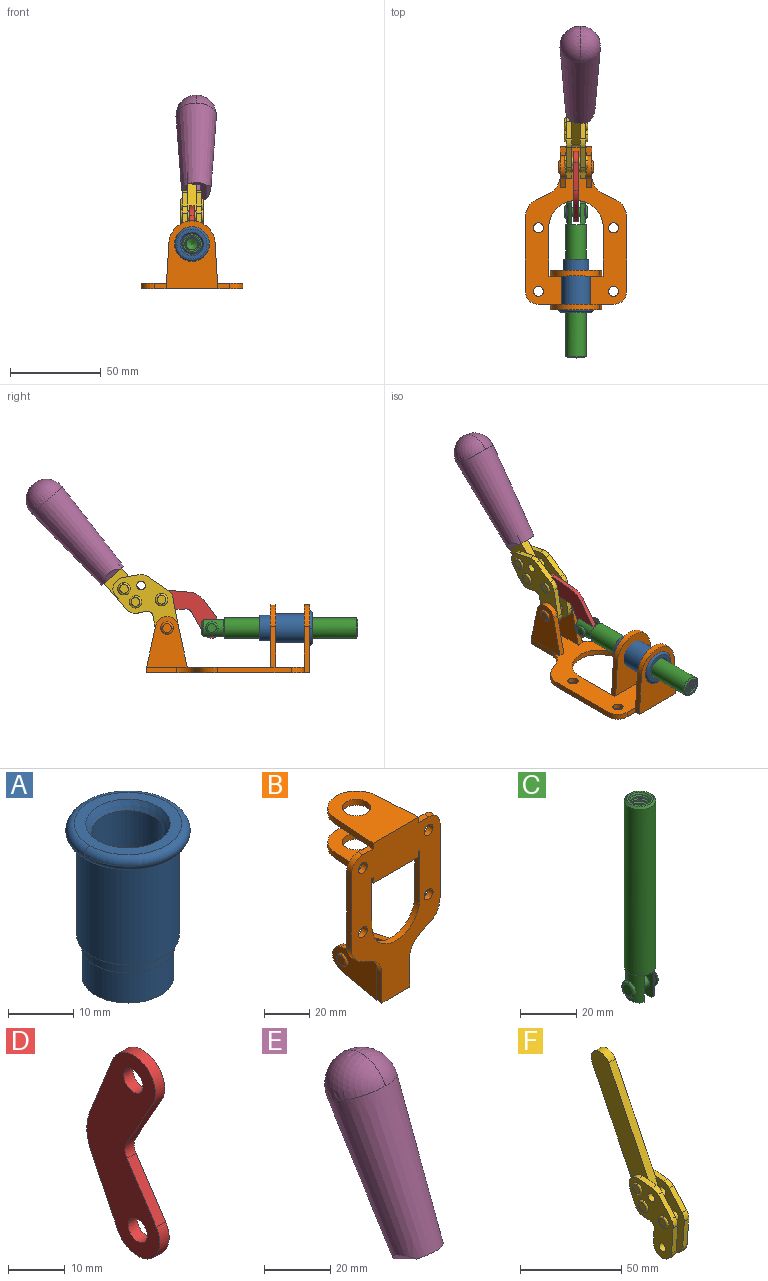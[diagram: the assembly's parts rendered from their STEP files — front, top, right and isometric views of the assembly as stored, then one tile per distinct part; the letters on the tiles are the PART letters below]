
ASSEMBLY  parts=6 mates=6
PART A: 15 faces, bbox 20.6x20.6x28.7 mm
  f0: torus R=8.26mm, axis (0,0,1), area 56.8mm2, adj f1,f10,f12
  f1: torus R=8.26mm, axis (0,0,1), area 56.8mm2, adj f0,f6,f13
  f2: cylinder r=5.59mm len=25.91mm, axis (0,0,1), area 909.6mm2, adj f3,f4
  f3: cone r=6.86mm half-angle=45deg, axis (0,0,-1), area 70.2mm2, adj f2,f14
  f4: cone r=6.47mm half-angle=30deg, axis (0,0,1), area 66.7mm2, adj f2,f13
  f5: cylinder r=7.04mm len=14.07mm, axis (0,0,1), area 252.6mm2, adj f11,f14
  f6: torus R=8.26mm, axis (0,0,1), area 56.8mm2, adj f1,f12,f13
  f7: cylinder r=7.16mm len=14.33mm, axis (0,0,1), area 91.5mm2, adj f9,f11
  f8: cylinder r=7.86mm len=18.42mm, axis (0,0,1), area 909.6mm2, adj f9,f10
  f9: plane 15.72x15.72mm, normal (0,0,-1), area 33mm2, adj f7,f8
  f10: plane 16.51x16.51mm, normal (0,0,-1), area 19.9mm2, adj f0,f8,f12
  f11: plane 14.33x14.33mm, normal (0,0,-1), area 5.7mm2, adj f5,f7
  f12: torus R=8.26mm, axis (0,0,1), area 56.8mm2, adj f0,f6,f10
  f13: plane 16.51x16.51mm, normal (0,0,1), area 82.7mm2, adj f1,f4,f6
  f14: plane 14.07x14.07mm, normal (0,0,-1), area 7.8mm2, adj f3,f5
PART B: 55 faces, bbox 55.7x37.4x89.8 mm
  f0: torus R=2.41mm, axis (-1,0,0), area 15mm2, adj f11,f15,f25
  f1: torus R=2.41mm, axis (-1,0,0), area 15mm2, adj f10,f12,f22
  f2: cylinder r=2.78mm len=5.56mm, axis (0,-1,0), area 54.2mm2, adj f30,f54
  f3: cylinder r=14.99mm len=29.97mm, axis (0,-1,0), area 145.9mm2, adj f30,f49,f53,f54
  f4: cylinder r=2.78mm len=5.56mm, axis (0,-1,0), area 54.2mm2, adj f30,f54
  f5: cylinder r=2.78mm len=5.56mm, axis (0,-1,0), area 54.2mm2, adj f30,f54
  f6: cylinder r=2.78mm len=5.56mm, axis (0,-1,0), area 54.2mm2, adj f30,f54
  f7: cylinder r=6.35mm len=12.7mm, axis (0,0,1), area 123.6mm2, adj f27,f51
  f8: cylinder r=6.35mm len=12.7mm, axis (0,0,-1), area 124.7mm2, adj f21,f35
  f9: cylinder r=2.41mm len=11.18mm, axis (-1,0,0), area 169.4mm2, adj f16,f19
  f10: plane 4.83x4.83mm, normal (1,0,0), area 18.3mm2, adj f1,f12
  f11: plane 4.83x4.83mm, normal (-1,0,0), area 18.3mm2, adj f0,f15
  f12: torus R=2.41mm, axis (-1,0,0), area 15mm2, adj f1,f10,f22
  f13: cylinder r=6.35mm len=12.41mm, axis (1,0,0), area 53.4mm2, adj f18,f19,f22,f23
  f14: cylinder r=6.35mm len=12.41mm, axis (-1,0,0), area 53.4mm2, adj f16,f17,f24,f25
  f15: torus R=2.41mm, axis (-1,0,0), area 15mm2, adj f0,f11,f25
  f16: plane 27.86x22.35mm, normal (1,0,0), area 425.4mm2, adj f9,f14,f17,f24,f30
  f17: plane 22.86x4.97mm, normal (0,0.21,0.98), area 72.5mm2, adj f14,f16,f25,f30
  f18: plane 22.86x4.97mm, normal (0,0.21,0.98), area 72.5mm2, adj f13,f19,f22,f30
  f19: plane 27.86x22.35mm, normal (-1,0,0), area 425.4mm2, adj f9,f13,f18,f23,f30
  f20: cylinder r=12.7mm len=25.35mm, axis (0,0,-1), area 119.8mm2, adj f21,f34,f35,f36
  f21: plane 34.21x28.07mm, normal (0,0,-1), area 702.4mm2, adj f8,f20,f30,f34,f36
  f22: plane 27.96x22.45mm, normal (1,0,0), area 407.2mm2, adj f1,f12,f13,f18,f23,f30,f42,f43
  f23: plane 22.86x4.97mm, normal (0,0.21,-0.98), area 72.5mm2, adj f13,f19,f22,f44
  f24: plane 22.86x4.97mm, normal (0,0.21,-0.98), area 72.5mm2, adj f14,f16,f25,f44
  f25: plane 27.86x22.35mm, normal (-1,0,0), area 407.1mm2, adj f0,f14,f15,f17,f24,f30,f45,f46
  f26: plane 3.1x0.95mm, normal (0,0,-1), area 2.7mm2, adj f30,f49,f50,f54
  f27: plane 34.21x28.07mm, normal (0,0,1), area 702.4mm2, adj f7,f28,f30,f50,f52
  f28: cylinder r=12.7mm len=25.35mm, axis (0,0,1), area 118.8mm2, adj f27,f50,f51,f52
  f29: plane 3.1x0.95mm, normal (0,0,-1), area 2.7mm2, adj f30,f52,f53,f54
  f30: plane 86.54x55.63mm, normal (0,1,0), area 2362.9mm2, adj f2,f3,f4,f5,f6,f16,f17,f18
  f31: plane 40.56x3.1mm, normal (-1,0,0), area 125.7mm2, adj f30,f32,f48,f54
  f32: cylinder r=7.11mm len=7.11mm, axis (0,-1,0), area 34.6mm2, adj f30,f31,f33,f54
  f33: plane 6.67x3.1mm, normal (0,0,1), area 20.4mm2, adj f30,f32,f34,f54
  f34: plane 25.39x3.13mm, normal (-1,0.06,0), area 79.5mm2, adj f20,f21,f33,f35,f54
  f35: plane 37.31x28.45mm, normal (0,0,1), area 789.9mm2, adj f8,f20,f34,f36,f54
  f36: plane 25.39x3.13mm, normal (1,0.06,0), area 79.5mm2, adj f20,f21,f35,f37,f54
  f37: plane 6.67x3.1mm, normal (0,0,1), area 20.4mm2, adj f30,f36,f38,f54
  f38: cylinder r=7.11mm len=7.11mm, axis (0,-1,0), area 34.6mm2, adj f30,f37,f39,f54
  f39: plane 40.56x3.1mm, normal (1,0,0), area 125.7mm2, adj f30,f38,f40,f54
  f40: cylinder r=11.18mm len=10.16mm, axis (0,-1,0), area 39.5mm2, adj f30,f39,f41,f54
  f41: plane 6.09x3.1mm, normal (0.42,0,-0.91), area 20.8mm2, adj f30,f40,f42,f54
  f42: cylinder r=11.18mm len=9.41mm, axis (0,-1,0), area 37.2mm2, adj f22,f30,f41,f43,f54
  f43: plane 16.5x3.1mm, normal (1,0,0), area 51.1mm2, adj f22,f42,f44,f54
  f44: plane 17.37x3.1mm, normal (0,0,-1), area 53.8mm2, adj f23,f24,f30,f43,f45,f54
  f45: plane 16.5x3.1mm, normal (-1,0,0), area 51.1mm2, adj f25,f44,f46,f54
  f46: cylinder r=11.18mm len=9.41mm, axis (0,-1,0), area 37.2mm2, adj f25,f30,f45,f47,f54
  f47: plane 6.09x3.1mm, normal (-0.42,0,-0.91), area 20.8mm2, adj f30,f46,f48,f54
  f48: cylinder r=11.18mm len=10.16mm, axis (0,-1,0), area 39.5mm2, adj f30,f31,f47,f54
  f49: plane 26.54x3.1mm, normal (-1,0,0), area 82.3mm2, adj f3,f26,f30,f54
  f50: plane 25.39x3.1mm, normal (1,0.06,0), area 78.8mm2, adj f26,f27,f28,f51,f54
  f51: plane 37.31x28.45mm, normal (0,0,-1), area 789.9mm2, adj f7,f28,f50,f52,f54
  f52: plane 25.39x3.1mm, normal (-1,0.06,0), area 78.8mm2, adj f27,f28,f29,f51,f54
  f53: plane 26.54x3.1mm, normal (1,0,0), area 82.3mm2, adj f3,f29,f30,f54
  f54: plane 89.66x55.63mm, normal (0,-1,0), area 2678.5mm2, adj f2,f3,f4,f5,f6,f26,f29,f31
PART C: 48 faces, bbox 12.6x11.1x86.1 mm
  f0: torus R=2.41mm, axis (-1,0,0), area 15mm2, adj f30,f32,f34
  f1: torus R=2.41mm, axis (-1,0,0), area 15mm2, adj f29,f31,f33
  f2: cylinder r=5.54mm len=72.39mm, axis (0,0,1), area 2518.5mm2, adj f3,f4,f42,f43
  f3: cone r=5.54mm half-angle=45deg, axis (0,0,1), area 7.6mm2, adj f2,f5,f41
  f4: cone r=5.54mm half-angle=45deg, axis (0,0,-1), area 34.9mm2, adj f2,f39
  f5: cylinder r=5.08mm len=11.48mm, axis (0,0,1), area 108.3mm2, adj f3,f7,f8,f41
  f6: cylinder r=2.41mm len=4.83mm, axis (-1,0,0), area 71.2mm2, adj f40,f41
  f7: cylinder r=2.41mm len=4.83mm, axis (-1,0,0), area 7.6mm2, adj f5,f34
  f8: cone r=5.08mm half-angle=45deg, axis (0,0,1), area 10.6mm2, adj f5,f37,f41
  f9: cone r=3.98mm half-angle=45deg, axis (0,0,1), area 17.6mm2, adj f27,f39,f45,f46,f47
  f10: cylinder r=2.41mm len=4.83mm, axis (-1,0,0), area 7.6mm2, adj f33,f38
  f11: cylinder r=3.2mm len=6.4mm, axis (0,0,1), area 78.4mm2, adj f12,f28,f44,f45,f47
  f12: cylinder r=3.2mm len=6.4mm, axis (0,0,1), area 10.5mm2, adj f11,f13,f45,f47
  f13: cylinder r=3.2mm len=6.4mm, axis (0,0,1), area 10.5mm2, adj f12,f14,f45,f47
  f14: cylinder r=3.2mm len=6.4mm, axis (0,0,1), area 10.5mm2, adj f13,f15,f45,f47
  f15: cylinder r=3.2mm len=6.4mm, axis (0,0,1), area 10.5mm2, adj f14,f16,f45,f47
  f16: cylinder r=3.2mm len=6.4mm, axis (0,0,1), area 10.5mm2, adj f15,f17,f45,f47
  f17: cylinder r=3.2mm len=6.4mm, axis (0,0,1), area 10.5mm2, adj f16,f18,f45,f47
  f18: cylinder r=3.2mm len=6.4mm, axis (0,0,1), area 10.5mm2, adj f17,f19,f45,f47
  f19: cylinder r=3.2mm len=6.4mm, axis (0,0,1), area 10.5mm2, adj f18,f20,f45,f47
  f20: cylinder r=3.2mm len=6.4mm, axis (0,0,1), area 10.5mm2, adj f19,f21,f45,f47
  f21: cylinder r=3.2mm len=6.4mm, axis (0,0,1), area 10.5mm2, adj f20,f22,f45,f47
  f22: cylinder r=3.2mm len=6.4mm, axis (0,0,1), area 10.5mm2, adj f21,f23,f45,f47
  f23: cylinder r=3.2mm len=6.4mm, axis (0,0,1), area 10.5mm2, adj f22,f24,f45,f47
  f24: cylinder r=3.2mm len=6.4mm, axis (0,0,1), area 10.5mm2, adj f23,f25,f45,f47
  f25: cylinder r=3.2mm len=6.4mm, axis (0,0,1), area 10.5mm2, adj f24,f26,f45,f47
  f26: cylinder r=3.2mm len=6.4mm, axis (0,0,1), area 10.5mm2, adj f25,f27,f45,f47
  f27: cylinder r=3.2mm len=6.4mm, axis (0,0,1), area 7.4mm2, adj f9,f26,f45,f47
  f28: cone r=3.2mm half-angle=60deg, axis (0,0,1), area 37.2mm2, adj f11
  f29: plane 4.83x4.83mm, normal (-1,0,0), area 18.3mm2, adj f1,f31
  f30: plane 4.83x4.83mm, normal (1,0,0), area 18.3mm2, adj f0,f32
  f31: torus R=2.41mm, axis (-1,0,0), area 15mm2, adj f1,f29,f33
  f32: torus R=2.41mm, axis (-1,0,0), area 15mm2, adj f0,f30,f34
  f33: plane 6.83x6.83mm, normal (1,0,0), area 18.3mm2, adj f1,f10,f31
  f34: plane 6.83x6.83mm, normal (-1,0,0), area 18.3mm2, adj f0,f7,f32
  f35: cone r=5.08mm half-angle=45deg, axis (0,0,1), area 10.6mm2, adj f36,f38,f40
  f36: plane 7.25x1.97mm, normal (0,0,-1), area 10mm2, adj f35,f40
  f37: plane 7.25x1.97mm, normal (0,0,-1), area 10mm2, adj f8,f41
  f38: cylinder r=5.08mm len=11.48mm, axis (0,0,1), area 108.3mm2, adj f10,f35,f40,f42
  f39: plane 9.55x9.55mm, normal (0,0,1), area 22mm2, adj f4,f9
  f40: plane 12.76x10.09mm, normal (1,0,0), area 95.7mm2, adj f6,f35,f36,f38,f42,f43
  f41: plane 12.76x10.09mm, normal (-1,0,0), area 95.7mm2, adj f3,f5,f6,f8,f37,f43
  f42: cone r=5.54mm half-angle=45deg, axis (0,0,1), area 7.6mm2, adj f2,f38,f40
  f43: plane 11.07x4.7mm, normal (0,0,-1), area 50.4mm2, adj f2,f40,f41
  f44: plane 0.89x0.62mm, normal (-1,0,0), area 0.3mm2, adj f11,f45,f46,f47
  f45: bspline ~24.8x7.63mm, area 266.6mm2, adj f9,f11,f12,f13,f14,f15,f16,f17
  f46: bspline ~24.87x7.63mm, area 73.6mm2, adj f9,f44,f45,f47
  f47: bspline ~24.98x7.63mm, area 272.5mm2, adj f9,f11,f12,f13,f14,f15,f16,f17
PART D: 12 faces, bbox 2.3x18.2x42.8 mm
  f0: cylinder r=2.4mm len=4.8mm, axis (1,0,0), area 34.9mm2, adj f4,f11
  f1: cylinder r=10.41mm len=8.47mm, axis (1,0,0), area 20.2mm2, adj f4,f9,f10,f11
  f2: cylinder r=3.05mm len=3.16mm, axis (1,0,0), area 7.7mm2, adj f4,f6,f7,f11
  f3: cylinder r=2.4mm len=4.8mm, axis (1,0,0), area 34.9mm2, adj f4,f11
  f4: plane 42.81x18.23mm, normal (-1,0,0), area 414.1mm2, adj f0,f1,f2,f3,f5,f6,f7,f8
  f5: cylinder r=5.54mm len=10.67mm, axis (1,0,0), area 41.8mm2, adj f4,f6,f10,f11
  f6: plane 11.66x6.53mm, normal (0,-0.87,-0.49), area 30.9mm2, adj f2,f4,f5,f11
  f7: plane 11.17x7.33mm, normal (0,-0.84,0.55), area 30.9mm2, adj f2,f4,f8,f11
  f8: cylinder r=5.54mm len=10.51mm, axis (1,0,0), area 41.8mm2, adj f4,f7,f9,f11
  f9: plane 13.67x6.67mm, normal (0,0.9,-0.44), area 35.1mm2, adj f1,f4,f8,f11
  f10: plane 14.1x5.7mm, normal (0,0.93,0.37), area 35.1mm2, adj f1,f4,f5,f11
  f11: plane 42.81x18.23mm, normal (1,0,0), area 414.1mm2, adj f0,f1,f2,f3,f5,f6,f7,f8
PART E: 11 faces, bbox 22.3x42.6x64.5 mm
  f0: sphere r=11.13mm, area 411.4mm2, adj f1,f8
  f1: cone r=11.11mm half-angle=3.3deg, axis (0,0.44,0.9), area 3251.8mm2, adj f0,f7,f8,f9,f10
  f2: cylinder r=6.16mm len=11.7mm, axis (1,0,0), area 89.5mm2, adj f3,f4,f5,f6
  f3: plane 60.23x36.75mm, normal (-1,0,0), area 763.6mm2, adj f2,f4,f6,f10
  f4: plane 51.37x25.05mm, normal (0,0.9,-0.44), area 264.2mm2, adj f2,f3,f5,f10
  f5: plane 60.23x36.75mm, normal (1,0,0), area 763.6mm2, adj f2,f4,f6,f10
  f6: plane 51.37x25.05mm, normal (0,-0.9,0.44), area 264.2mm2, adj f2,f3,f5,f10
  f7: plane 9.95x5.95mm, normal (0.71,-0.31,-0.64), area 25.8mm2, adj f1,f10
  f8: sphere r=11.13mm, area 411.4mm2, adj f0,f1
  f9: plane 9.95x5.95mm, normal (-0.71,-0.31,-0.64), area 25.8mm2, adj f1,f10
  f10: plane 14.27x11.38mm, normal (0,-0.44,-0.9), area 106.7mm2, adj f1,f3,f4,f5,f6,f7,f9
PART F: 59 faces, bbox 12.9x60.2x99.6 mm
  f0: torus R=2.39mm, axis (-1,0,0), area 14.9mm2, adj f20,f43,f51
  f1: torus R=2.39mm, axis (-1,0,0), area 14.9mm2, adj f19,f42,f51
  f2: torus R=2.39mm, axis (-1,0,0), area 14.9mm2, adj f18,f35,f51
  f3: torus R=2.39mm, axis (-1,0,0), area 14.9mm2, adj f14,f17,f23
  f4: torus R=2.39mm, axis (-1,0,0), area 14.9mm2, adj f13,f16,f23
  f5: torus R=2.39mm, axis (-1,0,0), area 14.9mm2, adj f12,f15,f23
  f6: cylinder r=2.39mm len=4.78mm, axis (1,0,0), area 46.5mm2, adj f48,f50,f51
  f7: cylinder r=2.39mm len=4.78mm, axis (1,0,0), area 46.5mm2, adj f50,f51
  f8: cylinder r=6.35mm len=12.68mm, axis (1,0,0), area 61.8mm2, adj f38,f39,f50,f51
  f9: cylinder r=2.39mm len=4.78mm, axis (-1,0,0), area 70.5mm2, adj f46,f50
  f10: cylinder r=2.39mm len=4.78mm, axis (-1,0,0), area 46.5mm2, adj f23,f45,f46
  f11: cylinder r=2.39mm len=4.78mm, axis (-1,0,0), area 46.5mm2, adj f23,f46
  f12: plane 4.78x4.78mm, normal (1,0,0), area 17.9mm2, adj f5,f15
  f13: plane 4.78x4.78mm, normal (1,0,0), area 17.9mm2, adj f4,f16
  f14: plane 4.78x4.78mm, normal (1,0,0), area 17.9mm2, adj f3,f17
  f15: torus R=2.39mm, axis (-1,0,0), area 14.9mm2, adj f5,f12,f23
  f16: torus R=2.39mm, axis (-1,0,0), area 14.9mm2, adj f4,f13,f23
  f17: torus R=2.39mm, axis (-1,0,0), area 14.9mm2, adj f3,f14,f23
  f18: plane 4.78x4.78mm, normal (-1,0,0), area 17.9mm2, adj f2,f35
  f19: plane 4.78x4.78mm, normal (-1,0,0), area 17.9mm2, adj f1,f42
  f20: plane 4.78x4.78mm, normal (-1,0,0), area 17.9mm2, adj f0,f43
  f21: plane 2.26x0.2mm, normal (1,0,0), area 0.2mm2, adj f31,f44
  f22: plane 2.26x0.2mm, normal (-1,0,0), area 0.2mm2, adj f41,f44
  f23: plane 39.37x30.77mm, normal (1,0,0), area 565.5mm2, adj f3,f4,f5,f10,f11,f15,f16,f17
  f24: cylinder r=6.1mm len=4.15mm, axis (-1,0,0), area 14.7mm2, adj f23,f25,f32,f46
  f25: plane 10.25x9.01mm, normal (0,-0.75,0.66), area 42.3mm2, adj f23,f24,f26,f46
  f26: cylinder r=6.35mm len=4.64mm, axis (-1,0,0), area 15.6mm2, adj f23,f25,f27,f46
  f27: plane 15.84x3.1mm, normal (0,-1,-0.07), area 49.2mm2, adj f23,f26,f28,f46
  f28: cylinder r=6.35mm len=12.68mm, axis (-1,0,0), area 61.8mm2, adj f23,f27,f29,f46
  f29: plane 8.11x3.1mm, normal (0,1,0.07), area 25.2mm2, adj f23,f28,f30,f46
  f30: cylinder r=3.05mm len=3.25mm, axis (-1,0,0), area 14.8mm2, adj f23,f29,f31,f46
  f31: plane 5.99x3.1mm, normal (0,0.07,-1), area 18.6mm2, adj f21,f23,f30,f44,f46
  f32: plane 9.5x3.1mm, normal (0,-0.07,1), area 29.5mm2, adj f23,f24,f33,f46,f47
  f33: cylinder r=6.1mm len=8.63mm, axis (-1,0,0), area 39.1mm2, adj f23,f32,f34,f47
  f34: plane 8.65x3.96mm, normal (0,0.91,-0.42), area 29.5mm2, adj f23,f33,f44,f47
  f35: torus R=2.39mm, axis (-1,0,0), area 14.9mm2, adj f2,f18,f51
  f36: plane 10.25x9.01mm, normal (0,-0.75,0.66), area 42.3mm2, adj f37,f49,f50,f51
  f37: cylinder r=6.35mm len=4.64mm, axis (1,0,0), area 15.6mm2, adj f36,f38,f50,f51
  f38: plane 15.84x3.1mm, normal (0,-1,-0.07), area 49.2mm2, adj f8,f37,f50,f51
  f39: plane 8.11x3.1mm, normal (0,1,0.07), area 25.2mm2, adj f8,f40,f50,f51
  f40: cylinder r=3.05mm len=3.25mm, axis (1,0,0), area 14.8mm2, adj f39,f41,f50,f51
  f41: plane 5.99x3.1mm, normal (0,0.07,-1), area 18.6mm2, adj f22,f40,f44,f50,f51
  f42: torus R=2.39mm, axis (-1,0,0), area 14.9mm2, adj f1,f19,f51
  f43: torus R=2.39mm, axis (-1,0,0), area 14.9mm2, adj f0,f20,f51
  f44: cylinder r=6.35mm len=12.12mm, axis (-1,0,0), area 128.9mm2, adj f21,f22,f23,f31,f34,f41,f46,f47
  f45: plane 2.65x1.35mm, normal (1,0,0), area 1mm2, adj f10,f55
  f46: plane 39.08x20.42mm, normal (-1,0,0), area 412.5mm2, adj f9,f10,f11,f24,f25,f26,f27,f28
  f47: plane 77.62x39.82mm, normal (1,0,0), area 850mm2, adj f32,f33,f34,f44,f53,f54,f55
  f48: plane 2.65x1.35mm, normal (-1,0,0), area 1mm2, adj f6,f55
  f49: cylinder r=6.1mm len=4.15mm, axis (1,0,0), area 14.7mm2, adj f36,f50,f51,f56
  f50: plane 39.08x20.42mm, normal (1,0,0), area 412.5mm2, adj f6,f7,f8,f9,f36,f37,f38,f39
  f51: plane 39.37x30.77mm, normal (-1,0,0), area 565.5mm2, adj f0,f1,f2,f6,f7,f8,f35,f36
  f52: plane 8.65x3.96mm, normal (0,0.91,-0.42), area 29.5mm2, adj f44,f51,f57,f58
  f53: plane 68.49x33.4mm, normal (0,0.9,-0.44), area 358.1mm2, adj f44,f47,f54,f58
  f54: cylinder r=6.35mm len=12.06mm, axis (1,0,0), area 93.7mm2, adj f47,f53,f55,f58
  f55: plane 68.49x33.4mm, normal (0,-0.9,0.44), area 358.1mm2, adj f44,f45,f46,f47,f48,f50,f54,f58
  f56: plane 9.5x3.1mm, normal (0,-0.07,1), area 29.5mm2, adj f49,f50,f51,f57,f58
  f57: cylinder r=6.1mm len=8.63mm, axis (1,0,0), area 39.1mm2, adj f51,f52,f56,f58
  f58: plane 77.62x39.82mm, normal (-1,0,0), area 850mm2, adj f44,f52,f53,f54,f55,f56,f57
PLACE A rot(axis=(1,0,0),90deg) t=(0,10.7,0)mm
PLACE B rot(axis=(1,0,0),90deg) t=(0,9.43,0)mm fixed
PLACE C rot(axis=(1,0,0),90deg) t=(0,32.36,0)mm
PLACE D rot(axis=(1,0,0),121.4deg) t=(0,42.92,11.66)mm
PLACE E rot(axis=(-1,0,0),15deg) t=(2.31,26.05,61.98)mm
PLACE F rot(axis=(-1,0,0),15deg) t=(0,26.05,61.98)mm
MATE revolute D.f5 <-> C.f6  axis (1,0,0) through (0,16.89,24.61)mm
MATE fastened F.f54 <-> E.f2  axis (1,0,0) through (0,108.85,96.5)mm
MATE fastened A.f2 <-> B.f7  axis (0,-1,0) through (0,-36.96,24.61)mm
MATE slider C.f2 <-> B.f7  axis (0,-1,0) through (0,-26.42,24.61)mm
MATE revolute D.f3 <-> F.f4  axis (1,0,0) through (0,44.55,40.2)mm
MATE revolute B.f0 <-> F.f7  axis (-1,0,0) through (0,41.52,24.61)mm
